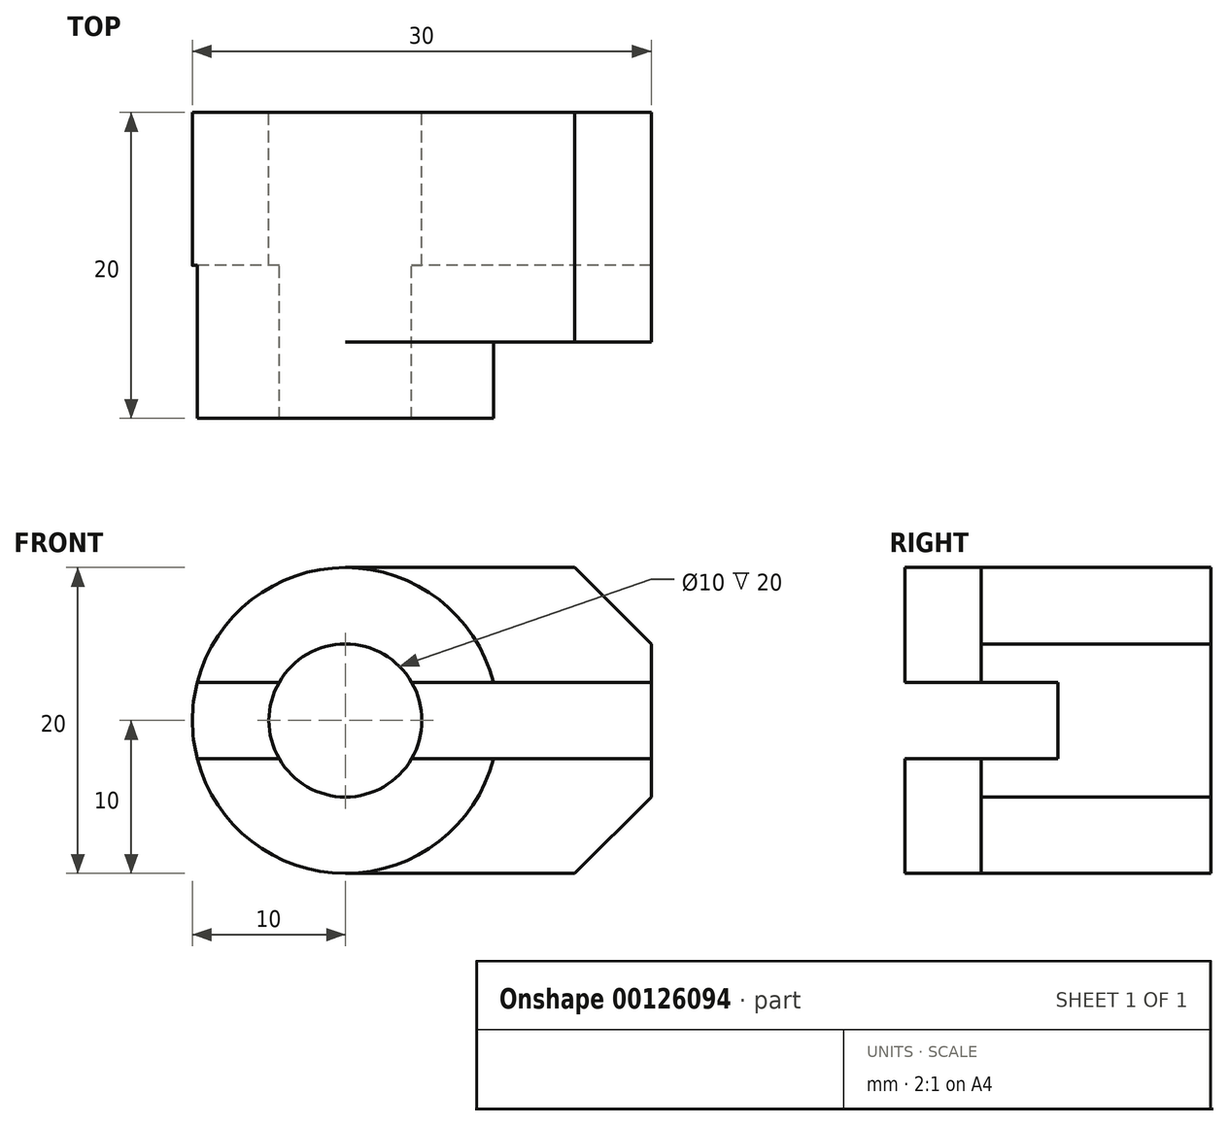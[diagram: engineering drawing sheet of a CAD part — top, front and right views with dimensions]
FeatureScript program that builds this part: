
annotation { "Feature Type Name" : "Feature", "Feature Type Description" : "" }
export const myFeature = defineFeature(function(context is Context, id is Id, definition is map)
    precondition{}
    {
        {
            var Q0;
            Q0=qCreatedBy(makeId("Front.planeOp"),FACE);
            var sketch = newSketch(context, id + "F0", { "sketchPlane" : qUnion([Q0])});
            skArc(sketch, "E0", {"start": v(9.68, 2.5) * mm, "mid": v(-10, 0) * mm, "end": v(9.68, -2.5) * mm});
            skCircle(sketch, "E1", {"center": v(0, 0) * mm, "radius": 5 * mm});
            skLineSegment(sketch, "E2", {"start": v(0, 10) * mm, "end": v(15, 10) * mm});
            skLineSegment(sketch, "E3", {"start": v(15, 10) * mm, "end": v(20, 5) * mm});
            skLineSegment(sketch, "E4", {"start": v(20, 5) * mm, "end": v(20, 2.5) * mm});
            skLineSegment(sketch, "E5", {"start": v(20, 2.5) * mm, "end": v(4.33, 2.5) * mm});
            skLineSegment(sketch, "E6.MirrorCS", {"start": v(15, -10) * mm, "end": v(20, -5) * mm});
            skLineSegment(sketch, "E7.MirrorCS", {"start": v(20, -2.5) * mm, "end": v(4.33, -2.5) * mm});
            skLineSegment(sketch, "E8.MirrorCS", {"start": v(0, -10) * mm, "end": v(15, -10) * mm});
            skLineSegment(sketch, "E9.MirrorCS", {"start": v(20, -5) * mm, "end": v(20, -2.5) * mm});
            skLineSegment(sketch, "E10", {"start": v(-4.33, 2.5) * mm, "end": v(-9.68, 2.5) * mm});
            skLineSegment(sketch, "E11", {"start": v(-4.33, -2.5) * mm, "end": v(-9.68, -2.5) * mm});
            skLineSegment(sketch, "E12", {"start": v(20, 2.5) * mm, "end": v(20, -2.5) * mm});
            skSolve(sketch);
        }
        {
            var Q0;
            {var subQ5=sQuery(id+"F0.wireOp",EDGE,"E10");Q0=makeQuery(id+"F0.imprint","IMPRINT",FACE,{"disambiguationData":[TD([[makeQuery(id+"F0.imprint","IMPRINT",EDGE,{"derivedFrom":subQ5}),-1.0]])]});}
            var Q1;
            {var subQ3=sQuery(id+"F0.wireOp",EDGE,"E11");Q1=makeQuery(id+"F0.imprint","IMPRINT",FACE,{"disambiguationData":[TD([[makeQuery(id+"F0.imprint","IMPRINT",EDGE,{"derivedFrom":subQ3}),1.0]])]});}
            extrude(context, id + "F1", {"entities" : qUnion([Q0, Q1]), "depth" : 10 * mm});
        }
        {
            var Q0;
            {var subQ1=sQuery(id+"F0.wireOp",EDGE,"E2");Q0=makeQuery(id+"F0.imprint","IMPRINT",FACE,{"disambiguationData":[TD([[makeQuery(id+"F0.imprint","IMPRINT",EDGE,{"derivedFrom":subQ1}),-1.0]])]});}
            var Q1;
            Q1=makeQuery(id+"F0.imprint","IMPRINT",FACE,{"disambiguationData":[TD([[makeQuery(id+"F0.imprint","IMPRINT",EDGE,{"derivedFrom":sQuery(id+"F0.wireOp",EDGE,"E6.MirrorCS")}),1.0]])]});
            var Q2;
            {var subQ3=sQuery(id+"F0.wireOp",EDGE,"E12");Q2=makeQuery(id+"F0.imprint","IMPRINT",FACE,{"disambiguationData":[TD([[makeQuery(id+"F0.imprint","IMPRINT",EDGE,{"derivedFrom":subQ3}),-1.0]])]});}
            var Q3;
            {var subQ5=sQuery(id+"F0.wireOp",EDGE,"E10");Q3=makeQuery(id+"F0.imprint","IMPRINT",FACE,{"disambiguationData":[TD([[makeQuery(id+"F0.imprint","IMPRINT",EDGE,{"derivedFrom":subQ5}),-1.0]])]});}
            var Q4;
            {var subQ0=sQuery(id+"F0.wireOp",EDGE,"E10");Q4=makeQuery(id+"F0.imprint","IMPRINT",FACE,{"disambiguationData":[TD([[makeQuery(id+"F0.imprint","IMPRINT",EDGE,{"derivedFrom":subQ0}),1.0]])]});}
            var Q5;
            {var subQ3=sQuery(id+"F0.wireOp",EDGE,"E11");Q5=makeQuery(id+"F0.imprint","IMPRINT",FACE,{"disambiguationData":[TD([[makeQuery(id+"F0.imprint","IMPRINT",EDGE,{"derivedFrom":subQ3}),1.0]])]});}
            extrude(context, id + "F2", {"entities" : qUnion([Q0, Q1, Q2, Q3, Q4, Q5]), "operationType" : NewBodyOperationType.ADD, "oppositeDirection" : true, "depth" : 10 * mm});
        }
        {
            var Q0;
            {var subQ1=sQuery(id+"F0.wireOp",EDGE,"E2");Q0=makeQuery(id+"F0.imprint","IMPRINT",FACE,{"disambiguationData":[TD([[makeQuery(id+"F0.imprint","IMPRINT",EDGE,{"derivedFrom":subQ1}),-1.0]])]});}
            var Q1;
            Q1=makeQuery(id+"F0.imprint","IMPRINT",FACE,{"disambiguationData":[TD([[makeQuery(id+"F0.imprint","IMPRINT",EDGE,{"derivedFrom":sQuery(id+"F0.wireOp",EDGE,"E6.MirrorCS")}),1.0]])]});
            extrude(context, id + "F3", {"entities" : qUnion([Q0, Q1]), "operationType" : NewBodyOperationType.ADD, "depth" : 5 * mm});
        }
    });
